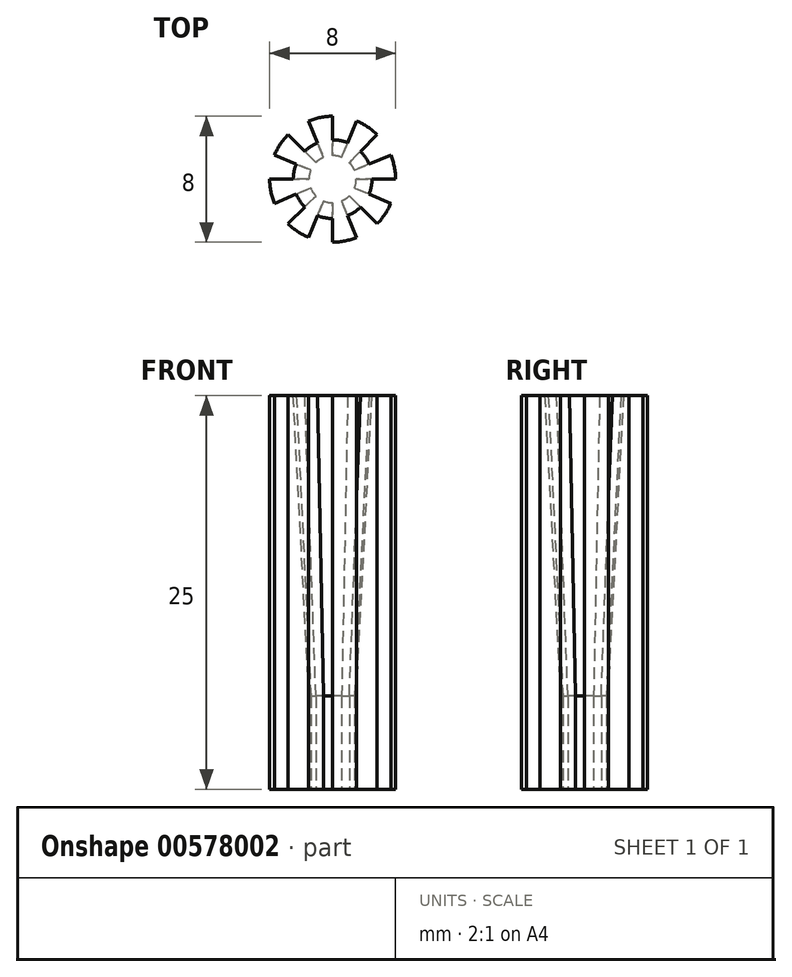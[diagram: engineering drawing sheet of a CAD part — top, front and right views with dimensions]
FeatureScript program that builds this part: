
annotation { "Feature Type Name" : "Feature", "Feature Type Description" : "" }
export const myFeature = defineFeature(function(context is Context, id is Id, definition is map)
    precondition{}
    {
        {
            var Q0;
            Q0=qCreatedBy(makeId("Top.planeOp"),FACE);
            var sketch = newSketch(context, id + "F0", { "sketchPlane" : qUnion([Q0])});
            skArc(sketch, "E0", {"start": v(-2.83, 2.83) * mm, "mid": v(-3.33, 2.22) * mm, "end": v(-3.7, 1.53) * mm});
            skLineSegment(sketch, "E1", {"start": v(0, 4) * mm, "end": v(0, 1.5) * mm});
            skLineSegment(sketch, "E2.1.0", {"start": v(-2.83, 2.83) * mm, "end": v(-1.06, 1.06) * mm});
            skLineSegment(sketch, "E2.2.0", {"start": v(-4, 0) * mm, "end": v(-1.5, 0) * mm});
            skLineSegment(sketch, "E2.3.0", {"start": v(-2.83, -2.83) * mm, "end": v(-1.06, -1.06) * mm});
            skLineSegment(sketch, "E2.4.0", {"start": v(0, -4) * mm, "end": v(0, -1.5) * mm});
            skLineSegment(sketch, "E2.5.0", {"start": v(2.83, -2.83) * mm, "end": v(1.06, -1.06) * mm});
            skLineSegment(sketch, "E2.6.0", {"start": v(4, 0) * mm, "end": v(1.5, 0) * mm});
            skLineSegment(sketch, "E2.7.0", {"start": v(2.83, 2.83) * mm, "end": v(1.06, 1.06) * mm});
            skLineSegment(sketch, "E3", {"start": v(0.57, 1.39) * mm, "end": v(1.53, 3.7) * mm});
            skLineSegment(sketch, "E4.1.0", {"start": v(-0.57, 1.39) * mm, "end": v(-1.53, 3.7) * mm});
            skLineSegment(sketch, "E4.2.0", {"start": v(-1.39, 0.57) * mm, "end": v(-3.7, 1.53) * mm});
            skLineSegment(sketch, "E4.3.0", {"start": v(-1.39, -0.57) * mm, "end": v(-3.7, -1.53) * mm});
            skLineSegment(sketch, "E4.4.0", {"start": v(-0.57, -1.39) * mm, "end": v(-1.53, -3.7) * mm});
            skLineSegment(sketch, "E4.5.0", {"start": v(0.57, -1.39) * mm, "end": v(1.53, -3.7) * mm});
            skLineSegment(sketch, "E4.6.0", {"start": v(1.39, -0.57) * mm, "end": v(3.7, -1.53) * mm});
            skLineSegment(sketch, "E4.7.0", {"start": v(1.39, 0.57) * mm, "end": v(3.7, 1.53) * mm});
            skArc(sketch, "E5", {"start": v(-1.39, 0.57) * mm, "mid": v(-1.47, 0.3) * mm, "end": v(-1.5, 0) * mm});
            skArc(sketch, "E6.trimOffspring", {"start": v(-4, 0) * mm, "mid": v(-3.92, -0.78) * mm, "end": v(-3.7, -1.53) * mm});
            skArc(sketch, "E7.trimOffspring", {"start": v(-2.83, -2.83) * mm, "mid": v(-2.22, -3.33) * mm, "end": v(-1.53, -3.7) * mm});
            skArc(sketch, "E8.trimOffspring", {"start": v(0, -4) * mm, "mid": v(0.78, -3.92) * mm, "end": v(1.53, -3.7) * mm});
            skArc(sketch, "E9.trimOffspring", {"start": v(2.83, -2.83) * mm, "mid": v(3.33, -2.22) * mm, "end": v(3.7, -1.53) * mm});
            skArc(sketch, "E10.trimOffspring", {"start": v(4, 0) * mm, "mid": v(3.92, 0.78) * mm, "end": v(3.7, 1.53) * mm});
            skArc(sketch, "E11.trimOffspring", {"start": v(2.83, 2.83) * mm, "mid": v(2.22, 3.33) * mm, "end": v(1.53, 3.7) * mm});
            skArc(sketch, "E12.trimOffspring", {"start": v(0, 4) * mm, "mid": v(-0.78, 3.92) * mm, "end": v(-1.53, 3.7) * mm});
            skArc(sketch, "E13.trimOffspring", {"start": v(-1.39, -0.57) * mm, "mid": v(-1.25, -0.83) * mm, "end": v(-1.06, -1.06) * mm});
            skArc(sketch, "E14.trimOffspring", {"start": v(-0.57, -1.39) * mm, "mid": v(-0.3, -1.47) * mm, "end": v(0, -1.5) * mm});
            skArc(sketch, "E15.trimOffspring", {"start": v(0.57, -1.39) * mm, "mid": v(0.83, -1.25) * mm, "end": v(1.06, -1.06) * mm});
            skArc(sketch, "E16.trimOffspring", {"start": v(1.39, -0.57) * mm, "mid": v(1.47, -0.3) * mm, "end": v(1.5, 0) * mm});
            skArc(sketch, "E17.trimOffspring", {"start": v(-0.57, 1.39) * mm, "mid": v(-0.83, 1.25) * mm, "end": v(-1.06, 1.06) * mm});
            skArc(sketch, "E18.trimOffspring", {"start": v(0.57, 1.39) * mm, "mid": v(0.3, 1.47) * mm, "end": v(0, 1.5) * mm});
            skArc(sketch, "E19.trimOffspring", {"start": v(1.39, 0.57) * mm, "mid": v(1.25, 0.83) * mm, "end": v(1.06, 1.06) * mm});
            skSolve(sketch);
        }
        {
            var Q0;
            Q0 = qSketchRegion(id + "F0", true);
            extrude(context, id + "F1", {"entities" : qUnion([Q0]), "depth" : 25 * mm, "offsetDistance" : 25 * mm});
        }
        {
            var Q0;
            Q0=makeQuery(id+"F1.opExtrude","CAP_FACE",FACE,{"disambiguationData":[OSD([sQuery(id+"F0.wireOp",EDGE,"E0"),sQuery(id+"F0.wireOp",EDGE,"E1"),sQuery(id+"F0.wireOp",EDGE,"E2.1.0"),sQuery(id+"F0.wireOp",EDGE,"E2.2.0"),sQuery(id+"F0.wireOp",EDGE,"E2.3.0"),sQuery(id+"F0.wireOp",EDGE,"E2.4.0"),sQuery(id+"F0.wireOp",EDGE,"E2.5.0"),sQuery(id+"F0.wireOp",EDGE,"E2.6.0"),sQuery(id+"F0.wireOp",EDGE,"E2.7.0"),sQuery(id+"F0.wireOp",EDGE,"E3"),sQuery(id+"F0.wireOp",EDGE,"E4.1.0"),sQuery(id+"F0.wireOp",EDGE,"E4.2.0"),sQuery(id+"F0.wireOp",EDGE,"E4.3.0"),sQuery(id+"F0.wireOp",EDGE,"E4.4.0"),sQuery(id+"F0.wireOp",EDGE,"E4.5.0"),sQuery(id+"F0.wireOp",EDGE,"E4.6.0"),sQuery(id+"F0.wireOp",EDGE,"E4.7.0"),sQuery(id+"F0.wireOp",EDGE,"E5"),sQuery(id+"F0.wireOp",EDGE,"E6.trimOffspring"),sQuery(id+"F0.wireOp",EDGE,"E7.trimOffspring"),sQuery(id+"F0.wireOp",EDGE,"E8.trimOffspring"),sQuery(id+"F0.wireOp",EDGE,"E9.trimOffspring"),sQuery(id+"F0.wireOp",EDGE,"E10.trimOffspring"),sQuery(id+"F0.wireOp",EDGE,"E11.trimOffspring"),sQuery(id+"F0.wireOp",EDGE,"E12.trimOffspring"),sQuery(id+"F0.wireOp",EDGE,"E13.trimOffspring"),sQuery(id+"F0.wireOp",EDGE,"E14.trimOffspring"),sQuery(id+"F0.wireOp",EDGE,"E15.trimOffspring"),sQuery(id+"F0.wireOp",EDGE,"E16.trimOffspring"),sQuery(id+"F0.wireOp",EDGE,"E17.trimOffspring"),sQuery(id+"F0.wireOp",EDGE,"E18.trimOffspring"),sQuery(id+"F0.wireOp",EDGE,"E19.trimOffspring")])],"isStart":false});
            var sketch = newSketch(context, id + "F2", { "sketchPlane" : qUnion([Q0])});
            skCircle(sketch, "E20", {"center": v(0, 0) * mm, "radius": 2.5 * mm});
            skSolve(sketch);
        }
        {
            var Q0;
            Q0 = qSketchRegion(id + "F2", true);
            extrude(context, id + "F3", {"entities" : qUnion([Q0]), "operationType" : NewBodyOperationType.ADD, "oppositeDirection" : true, "depth" : 25 * mm, "offsetDistance" : 25 * mm, "hasDraft" : true, "draftAngle" : 3 * degree, "draftPullDirection" : true});
        }
    });
